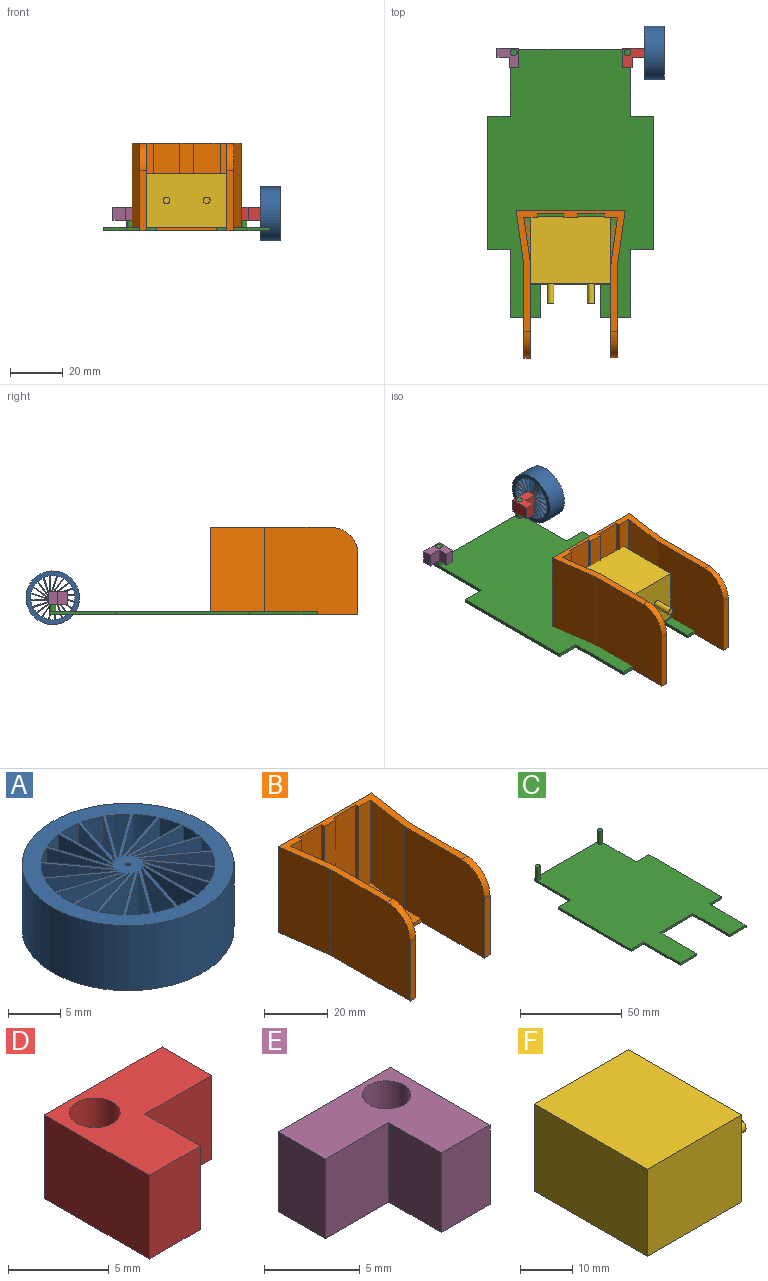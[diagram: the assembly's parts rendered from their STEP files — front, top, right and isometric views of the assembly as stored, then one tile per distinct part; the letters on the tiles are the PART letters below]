
ASSEMBLY  parts=6 mates=7
PART A: 64 faces, bbox 20.3x20.3x7.6 mm
  f0: plane 7.62x6.95mm, normal (0.31,0.95,0), area 55.7mm2, adj f2,f3,f6,f8
  f1: plane 7.62x6.69mm, normal (-0.31,-0.95,0), area 53.6mm2, adj f2,f3,f4,f5
  f2: plane 20.32x20.32mm, normal (0,0,1), area 162.9mm2, adj f0,f1,f4,f5,f6,f7,f8,f9
  f3: plane 20.32x20.32mm, normal (0,0,-1), area 162.9mm2, adj f0,f1,f4,f5,f6,f7,f8,f9
  f4: cylinder r=8.31mm len=7.62mm, axis (0,0,-1), area 17.3mm2, adj f1,f2,f3,f5
  f5: plane 7.62x5.91mm, normal (0.59,0.81,0), area 55.7mm2, adj f1,f2,f3,f4
  f6: plane 7.62x7.04mm, normal (0,-1,0), area 53.6mm2, adj f0,f2,f3,f8
  f7: plane 7.62x7.31mm, normal (0,1,0), area 55.7mm2, adj f2,f3,f9,f11
  f8: cylinder r=8.31mm len=7.62mm, axis (0,0,-1), area 17.3mm2, adj f0,f2,f3,f6
  f9: plane 7.62x6.69mm, normal (0.31,-0.95,0), area 53.6mm2, adj f2,f3,f7,f11
  f10: plane 7.62x6.95mm, normal (-0.31,0.95,0), area 55.7mm2, adj f2,f3,f12,f14
  f11: cylinder r=8.31mm len=7.62mm, axis (0,0,-1), area 17.3mm2, adj f2,f3,f7,f9
  f12: plane 7.62x5.69mm, normal (0.59,-0.81,0), area 53.6mm2, adj f2,f3,f10,f14
  f13: plane 7.62x5.91mm, normal (-0.59,0.81,0), area 55.7mm2, adj f2,f3,f25,f58
  f14: cylinder r=8.31mm len=7.62mm, axis (0,0,-1), area 17.3mm2, adj f2,f3,f10,f12
  f15: plane 7.62x6.95mm, normal (-0.95,0.31,0), area 55.7mm2, adj f2,f3,f26,f60
  f16: plane 7.62x6.69mm, normal (0.95,-0.31,0), area 53.6mm2, adj f2,f3,f17,f18
  f17: plane 7.62x5.91mm, normal (-0.81,0.59,0), area 55.7mm2, adj f2,f3,f16,f18
  f18: cylinder r=8.31mm len=7.62mm, axis (0,0,-1), area 17.3mm2, adj f2,f3,f16,f17
  f19: plane 7.62x5.91mm, normal (-0.81,-0.59,0), area 55.7mm2, adj f2,f3,f24,f28
  f20: plane 7.62x5.69mm, normal (0.81,0.59,0), area 53.6mm2, adj f2,f3,f21,f22
  f21: plane 7.62x6.95mm, normal (-0.95,-0.31,0), area 55.7mm2, adj f2,f3,f20,f22
  f22: cylinder r=8.31mm len=7.62mm, axis (0,0,-1), area 17.3mm2, adj f2,f3,f20,f21
  f23: cylinder r=0.23mm len=7.62mm, axis (0,0,-1), area 11.1mm2, adj f2,f3
  f24: plane 7.62x5.69mm, normal (0.59,0.81,0), area 53.6mm2, adj f2,f3,f19,f28
  f25: plane 7.62x5.69mm, normal (0.81,-0.59,0), area 53.6mm2, adj f2,f3,f13,f58
  f26: plane 7.62x7.04mm, normal (1,0,0), area 53.6mm2, adj f2,f3,f15,f60
  f27: plane 7.62x5.91mm, normal (-0.59,-0.81,0), area 55.7mm2, adj f2,f3,f30,f31
  f28: cylinder r=8.31mm len=7.62mm, axis (0,0,-1), area 17.3mm2, adj f2,f3,f19,f24
  f29: plane 7.62x6.95mm, normal (-0.31,-0.95,0), area 55.7mm2, adj f2,f3,f33,f34
  f30: plane 7.62x6.69mm, normal (0.31,0.95,0), area 53.6mm2, adj f2,f3,f27,f31
  f31: cylinder r=8.31mm len=7.62mm, axis (0,0,-1), area 17.3mm2, adj f2,f3,f27,f30
  f32: plane 7.62x7.31mm, normal (0,-1,0), area 55.7mm2, adj f2,f3,f36,f37
  f33: plane 7.62x7.04mm, normal (0,1,0), area 53.6mm2, adj f2,f3,f29,f34
  f34: cylinder r=8.31mm len=7.62mm, axis (0,0,-1), area 17.3mm2, adj f2,f3,f29,f33
  f35: plane 7.62x6.95mm, normal (0.31,-0.95,0), area 55.7mm2, adj f2,f3,f39,f40
  f36: plane 7.62x6.69mm, normal (-0.31,0.95,0), area 53.6mm2, adj f2,f3,f32,f37
  f37: cylinder r=8.31mm len=7.62mm, axis (0,0,-1), area 17.3mm2, adj f2,f3,f32,f36
  f38: plane 7.62x5.91mm, normal (0.59,-0.81,0), area 55.7mm2, adj f2,f3,f42,f43
  f39: plane 7.62x5.69mm, normal (-0.59,0.81,0), area 53.6mm2, adj f2,f3,f35,f40
  f40: cylinder r=8.31mm len=7.62mm, axis (0,0,-1), area 17.3mm2, adj f2,f3,f35,f39
  f41: plane 7.62x5.91mm, normal (0.81,-0.59,0), area 55.7mm2, adj f2,f3,f45,f46
  f42: plane 7.62x5.69mm, normal (-0.81,0.59,0), area 53.6mm2, adj f2,f3,f38,f43
  f43: cylinder r=8.31mm len=7.62mm, axis (0,0,-1), area 17.3mm2, adj f2,f3,f38,f42
  f44: plane 7.62x6.95mm, normal (0.95,-0.31,0), area 55.7mm2, adj f2,f3,f48,f49
  f45: plane 7.62x6.69mm, normal (-0.95,0.31,0), area 53.6mm2, adj f2,f3,f41,f46
  f46: cylinder r=8.31mm len=7.62mm, axis (0,0,-1), area 17.3mm2, adj f2,f3,f41,f45
  f47: plane 7.62x7.31mm, normal (1,0,0), area 55.7mm2, adj f2,f3,f56,f57
  f48: plane 7.62x7.04mm, normal (-1,0,0), area 53.6mm2, adj f2,f3,f44,f49
  f49: cylinder r=8.31mm len=7.62mm, axis (0,0,-1), area 17.3mm2, adj f2,f3,f44,f48
  f50: plane 7.62x5.91mm, normal (0.81,0.59,0), area 55.7mm2, adj f2,f3,f54,f55
  f51: plane 7.62x5.69mm, normal (-0.81,-0.59,0), area 53.6mm2, adj f2,f3,f52,f53
  f52: plane 7.62x6.95mm, normal (0.95,0.31,0), area 55.7mm2, adj f2,f3,f51,f53
  f53: cylinder r=8.31mm len=7.62mm, axis (0,0,-1), area 17.3mm2, adj f2,f3,f51,f52
  f54: plane 7.62x5.69mm, normal (-0.59,-0.81,0), area 53.6mm2, adj f2,f3,f50,f55
  f55: cylinder r=8.31mm len=7.62mm, axis (0,0,-1), area 17.3mm2, adj f2,f3,f50,f54
  f56: plane 7.62x6.69mm, normal (-0.95,-0.31,0), area 53.6mm2, adj f2,f3,f47,f57
  f57: cylinder r=8.31mm len=7.62mm, axis (0,0,-1), area 17.3mm2, adj f2,f3,f47,f56
  f58: cylinder r=8.31mm len=7.62mm, axis (0,0,-1), area 17.3mm2, adj f2,f3,f13,f25
  f59: plane 7.62x7.31mm, normal (-1,0,0), area 55.7mm2, adj f2,f3,f61,f63
  f60: cylinder r=8.31mm len=7.62mm, axis (0,0,-1), area 17.3mm2, adj f2,f3,f15,f26
  f61: cylinder r=8.31mm len=7.62mm, axis (0,0,-1), area 17.3mm2, adj f2,f3,f59,f63
  f62: cylinder r=10.16mm len=20.32mm, axis (0,0,-1), area 486.4mm2, adj f2,f3
  f63: plane 7.62x6.69mm, normal (0.95,0.31,0), area 53.6mm2, adj f2,f3,f59,f61
PART B: 28 faces, bbox 41.4x55.9x33 mm
  f0: plane 35.56x33.02mm, normal (1,0,0), area 1142.4mm2, adj f1,f4,f9,f22,f23,f24,f27
  f1: plane 55.88x41.42mm, normal (0,0,-1), area 1169.7mm2, adj f0,f5,f6,f7,f8,f12,f13,f14
  f2: plane 31.75x5.06mm, normal (0,-1,0), area 160.8mm2, adj f4,f9,f18,f23
  f3: plane 31.75x5.11mm, normal (0,-1,0), area 162.3mm2, adj f4,f15,f17,f23
  f4: plane 45.72x41.42mm, normal (0,0,1), area 298.7mm2, adj f0,f2,f3,f5,f6,f7,f8,f9
  f5: plane 41.42x33.02mm, normal (0,1,0), area 1367.6mm2, adj f1,f4,f6,f13
  f6: plane 33.02x20.5mm, normal (-0.99,-0.14,0), area 683.8mm2, adj f1,f4,f5,f7
  f7: plane 35.38x33.02mm, normal (-1,0,0), area 1146.1mm2, adj f1,f4,f6,f24,f27
  f8: plane 35.38x33.02mm, normal (1,0,0), area 1146.1mm2, adj f1,f4,f13,f25,f26
  f9: plane 31.75x17.78mm, normal (0.99,0.14,0), area 570.2mm2, adj f0,f2,f4,f23
  f10: plane 31.75x5.06mm, normal (0,-1,0), area 160.8mm2, adj f4,f11,f14,f23
  f11: plane 31.75x17.78mm, normal (-0.99,0.14,0), area 570.2mm2, adj f4,f10,f12,f23
  f12: plane 35.56x33.02mm, normal (-1,0,0), area 1142.4mm2, adj f1,f4,f11,f22,f23,f25,f26
  f13: plane 33.02x20.5mm, normal (0.99,-0.14,0), area 683.8mm2, adj f1,f4,f5,f8
  f14: plane 33.02x1.27mm, normal (-1,0,0), area 41.9mm2, adj f1,f4,f10,f16,f21
  f15: plane 33.02x1.27mm, normal (1,0,0), area 41.9mm2, adj f1,f3,f4,f16,f21
  f16: plane 33.02x10.16mm, normal (0,-1,0), area 335.5mm2, adj f1,f4,f14,f15
  f17: plane 33.02x1.27mm, normal (-1,0,0), area 41.9mm2, adj f1,f3,f4,f19,f20
  f18: plane 33.02x1.27mm, normal (1,0,0), area 41.9mm2, adj f1,f2,f4,f19,f20
  f19: plane 33.02x10.16mm, normal (0,-1,0), area 335.5mm2, adj f1,f4,f17,f18
  f20: plane 10.16x1.27mm, normal (0,1,0), area 12.9mm2, adj f1,f17,f18,f23
  f21: plane 10.16x1.27mm, normal (0,1,0), area 12.9mm2, adj f1,f14,f15,f23
  f22: plane 30.48x1.27mm, normal (0,-1,0), area 38.7mm2, adj f0,f1,f12,f23
  f23: plane 35.56x25.4mm, normal (0,0,1), area 819.4mm2, adj f0,f2,f3,f9,f10,f11,f12,f20
  f24: plane 22.86x2.54mm, normal (0,-1,0), area 58.1mm2, adj f0,f1,f7,f27
  f25: plane 22.86x2.54mm, normal (0,-1,0), area 58.1mm2, adj f1,f8,f12,f26
  f26: cylinder r=10.16mm len=10.16mm, axis (-1,0,0), area 40.5mm2, adj f4,f8,f12,f25
  f27: cylinder r=10.16mm len=10.16mm, axis (-1,0,0), area 40.5mm2, adj f0,f4,f7,f24
PART C: 24 faces, bbox 63.1x101.6x8.9 mm
  f0: plane 8.68x1.27mm, normal (0,1,0), area 11mm2, adj f5,f16,f17,f21
  f1: plane 1.27x1.27mm, normal (0,0,1), area 0.3mm2, adj f4,f21,f22
  f2: plane 1.27x1.27mm, normal (0,0,1), area 0.3mm2, adj f3,f4,f18
  f3: plane 25.49x1.27mm, normal (1,0,0), area 32.4mm2, adj f2,f4,f15,f16,f17
  f4: plane 45.72x1.27mm, normal (0,1,0), area 58.1mm2, adj f1,f2,f3,f16,f17,f21
  f5: plane 50.61x1.27mm, normal (-1,0,0), area 64.3mm2, adj f0,f6,f16,f17
  f6: plane 8.68x1.27mm, normal (0,-1,0), area 11mm2, adj f5,f16,f17,f20
  f7: plane 11.43x1.27mm, normal (0,-1,0), area 14.5mm2, adj f8,f16,f17,f20
  f8: plane 25.49x1.27mm, normal (1,0,0), area 32.4mm2, adj f7,f9,f16,f17
  f9: plane 22.86x1.27mm, normal (0,-1,0), area 29mm2, adj f8,f10,f16,f17
  f10: plane 25.49x1.27mm, normal (-1,0,0), area 32.4mm2, adj f9,f11,f16,f17
  f11: plane 11.43x1.27mm, normal (0,-1,0), area 14.5mm2, adj f10,f12,f16,f17
  f12: plane 25.49x1.27mm, normal (1,0,0), area 32.4mm2, adj f11,f13,f16,f17
  f13: plane 8.68x1.27mm, normal (0,-1,0), area 11mm2, adj f12,f14,f16,f17
  f14: plane 50.61x1.27mm, normal (1,0,0), area 64.3mm2, adj f13,f15,f16,f17
  f15: plane 8.68x1.27mm, normal (0,1,0), area 11mm2, adj f3,f14,f16,f17
  f16: plane 101.6x63.07mm, normal (0,0,1), area 4929.9mm2, adj f0,f3,f4,f5,f6,f7,f8,f9
  f17: plane 101.6x63.07mm, normal (0,0,-1), area 4940.7mm2, adj f0,f3,f4,f5,f6,f7,f8,f9
  f18: cylinder r=1.27mm len=7.62mm, axis (0,0,-1), area 60.8mm2, adj f2,f16,f19
  f19: plane 2.54x2.54mm, normal (0,0,1), area 5.1mm2, adj f18
  f20: plane 25.49x1.27mm, normal (-1,0,0), area 32.4mm2, adj f6,f7,f16,f17
  f21: plane 25.49x1.27mm, normal (-1,0,0), area 32.4mm2, adj f0,f1,f4,f16,f17
  f22: cylinder r=1.27mm len=7.62mm, axis (0,0,-1), area 60.8mm2, adj f1,f16,f23
  f23: plane 2.54x2.54mm, normal (0,0,1), area 5.1mm2, adj f22
PART D: 9 faces, bbox 8.3x7.4x5.1 mm
  f0: plane 8.26x5.08mm, normal (0,1,0), area 42mm2, adj f1,f5,f7,f8
  f1: plane 7.37x5.08mm, normal (-1,0,0), area 37.4mm2, adj f0,f2,f7,f8
  f2: plane 5.08x3.58mm, normal (0,-1,0), area 18.2mm2, adj f1,f3,f7,f8
  f3: plane 5.08x3.89mm, normal (1,0,0), area 19.8mm2, adj f2,f4,f7,f8
  f4: plane 5.08x4.68mm, normal (0,-1,0), area 23.8mm2, adj f3,f5,f7,f8
  f5: plane 5.08x3.47mm, normal (1,0,0), area 17.6mm2, adj f0,f4,f7,f8
  f6: cylinder r=1.27mm len=5.08mm, axis (0,0,-1), area 40.5mm2, adj f7,f8
  f7: plane 8.26x7.37mm, normal (0,0,1), area 37.6mm2, adj f0,f1,f2,f3,f4,f5,f6
  f8: plane 8.26x7.37mm, normal (0,0,-1), area 37.6mm2, adj f0,f1,f2,f3,f4,f5,f6
PART E: 9 faces, bbox 8.3x7.4x5.1 mm
  f0: plane 8.26x5.08mm, normal (0,1,0), area 42mm2, adj f1,f5,f7,f8
  f1: plane 7.37x5.08mm, normal (1,0,0), area 37.4mm2, adj f0,f2,f7,f8
  f2: plane 5.08x3.58mm, normal (0,-1,0), area 18.2mm2, adj f1,f3,f7,f8
  f3: plane 5.08x3.89mm, normal (-1,0,0), area 19.8mm2, adj f2,f4,f7,f8
  f4: plane 5.08x4.68mm, normal (0,-1,0), area 23.8mm2, adj f3,f5,f7,f8
  f5: plane 5.08x3.47mm, normal (-1,0,0), area 17.6mm2, adj f0,f4,f7,f8
  f6: cylinder r=1.27mm len=5.08mm, axis (0,0,-1), area 40.5mm2, adj f7,f8
  f7: plane 8.26x7.37mm, normal (0,0,1), area 37.6mm2, adj f0,f1,f2,f3,f4,f5,f6
  f8: plane 8.26x7.37mm, normal (0,0,-1), area 37.6mm2, adj f0,f1,f2,f3,f4,f5,f6
PART F: 10 faces, bbox 33x30.5x20.3 mm
  f0: plane 25.4x20.32mm, normal (0,1,0), area 516.1mm2, adj f1,f3,f4,f5
  f1: plane 30.48x20.32mm, normal (-1,0,0), area 619.4mm2, adj f0,f2,f4,f5
  f2: plane 25.4x20.32mm, normal (0,-1,0), area 516.1mm2, adj f1,f3,f4,f5
  f3: plane 30.48x20.32mm, normal (1,0,0), area 609.2mm2, adj f0,f2,f4,f5,f6,f8
  f4: plane 30.48x25.4mm, normal (0,0,1), area 774.2mm2, adj f0,f1,f2,f3
  f5: plane 30.48x25.4mm, normal (0,0,-1), area 774.2mm2, adj f0,f1,f2,f3
  f6: cylinder r=1.27mm len=7.62mm, axis (-1,0,0), area 60.8mm2, adj f3,f7
  f7: plane 2.54x2.54mm, normal (1,0,0), area 5.1mm2, adj f6
  f8: cylinder r=1.27mm len=7.62mm, axis (-1,0,0), area 60.8mm2, adj f3,f9
  f9: plane 2.54x2.54mm, normal (1,0,0), area 5.1mm2, adj f8
PLACE A rot(axis=(0.58,-0.58,-0.58),120deg) t=(-234.49,121.26,-48.58)mm
PLACE B t=(-270.07,-10.23,7.74)mm
PLACE C t=(-270.07,28.15,7.74)mm
PLACE D t=(-257.39,17.03,11.55)mm
PLACE E t=(-282.76,17.03,11.55)mm
PLACE F rot(axis=(0.71,-0.71,0),180deg) t=(-243.77,59.43,29.33)mm
MATE fastened C.f16 <-> F.f4  axis (0,0,1) through (-270.07,2.84,9.01)mm
MATE fastened B.f23 <-> F.f4  axis (0,0,1) through (-270.07,2.84,9.01)mm
MATE revolute D.f6 <-> C.f18  axis (0,0,1) through (-248.48,77.68,16.63)mm
MATE revolute A.f4 <-> D.f5  axis (1,0,0) through (-242.11,77.58,14.09)mm
MATE revolute E.f6 <-> C.f22  axis (0,0,1) through (-291.66,77.68,16.63)mm
MATE fastened B.f1 <-> B.f5  axis (0,0,-1) through (-270.07,0.45,7.74)mm
MATE fastened D.f5 <-> A.f4  axis (1,0,0) through (-242.11,77.58,14.09)mm
